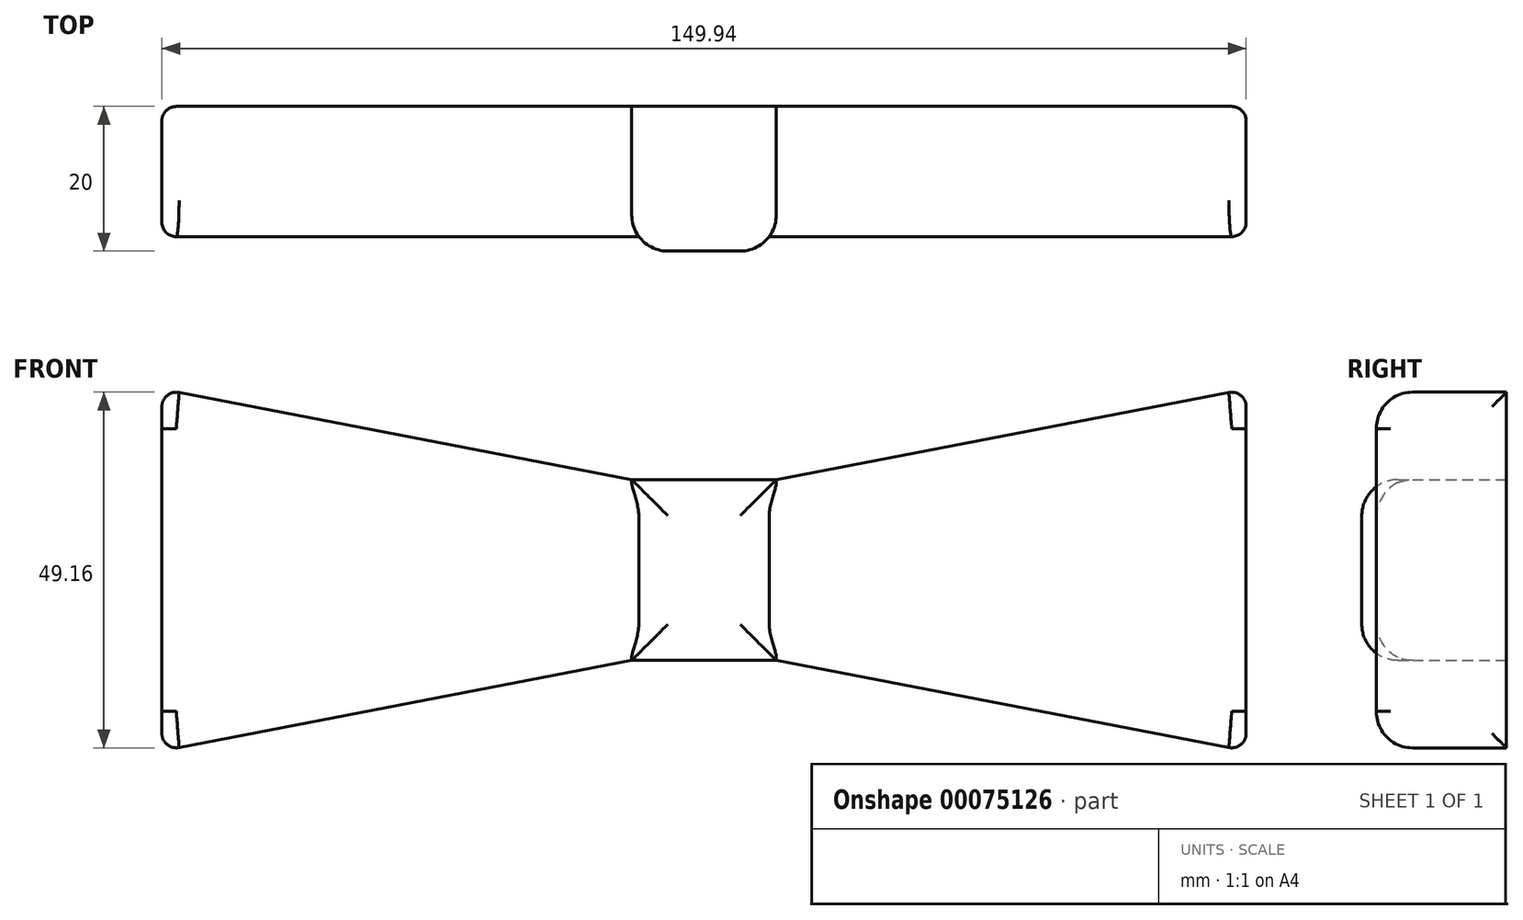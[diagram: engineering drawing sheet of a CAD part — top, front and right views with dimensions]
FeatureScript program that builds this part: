
annotation { "Feature Type Name" : "Feature", "Feature Type Description" : "" }
export const myFeature = defineFeature(function(context is Context, id is Id, definition is map)
    precondition{}
    {
        {
            var Q0;
            Q0=qCreatedBy(makeId("Front.planeOp"),FACE);
            var sketch = newSketch(context, id + "F0", { "sketchPlane" : qUnion([Q0])});
            skLineSegment(sketch, "E0.rect.bottom", {"start": v(10, -12.5) * mm, "end": v(-10, -12.5) * mm});
            skLineSegment(sketch, "E0.rect.top", {"start": v(10, 12.5) * mm, "end": v(-10, 12.5) * mm});
            skLineSegment(sketch, "E0.rect.left", {"start": v(10, -12.5) * mm, "end": v(10, 12.5) * mm});
            skLineSegment(sketch, "E0.rect.right", {"start": v(-10, -12.5) * mm, "end": v(-10, 12.5) * mm});
            skPoint(sketch, "E0.rect.middle", {"position": v(0, 0) * mm});
            skLineSegment(sketch, "E1", {"start": v(-10, 12.5) * mm, "end": v(-74.97, 25) * mm});
            skLineSegment(sketch, "E2", {"start": v(-74.97, 25) * mm, "end": v(-74.97, -25) * mm});
            skLineSegment(sketch, "E3", {"start": v(-74.97, -25) * mm, "end": v(-10, -12.5) * mm});
            skLineSegment(sketch, "E4.MirrorCS", {"start": v(10, 12.5) * mm, "end": v(74.97, 25) * mm});
            skLineSegment(sketch, "E5.MirrorCS", {"start": v(74.97, 25) * mm, "end": v(74.97, -25) * mm});
            skLineSegment(sketch, "E6.MirrorCS", {"start": v(74.97, -25) * mm, "end": v(10, -12.5) * mm});
            skSolve(sketch);
        }
        {
            var Q0;
            Q0=makeQuery(id+"F0.imprint","IMPRINT",FACE,{"disambiguationData":[TD([[makeQuery(id+"F0.imprint","IMPRINT",EDGE,{"derivedFrom":sQuery(id+"F0.wireOp",EDGE,"E0.rect.bottom")}),-1.0]])]});
            extrude(context, id + "F1", {"entities" : qUnion([Q0]), "depth" : 20 * mm});
        }
        {
            var Q0;
            Q0=makeQuery(id+"F0.imprint","IMPRINT",FACE,{"disambiguationData":[TD([[makeQuery(id+"F0.imprint","IMPRINT",EDGE,{"derivedFrom":sQuery(id+"F0.wireOp",EDGE,"E0.rect.left")}),-1.0]])]});
            var Q1;
            Q1=makeQuery(id+"F0.imprint","IMPRINT",FACE,{"disambiguationData":[TD([[makeQuery(id+"F0.imprint","IMPRINT",EDGE,{"derivedFrom":sQuery(id+"F0.wireOp",EDGE,"E0.rect.right")}),1.0]])]});
            extrude(context, id + "F2", {"entities" : qUnion([Q0, Q1]), "operationType" : NewBodyOperationType.ADD, "depth" : 18 * mm});
        }
        {
            var Q0;
            Q0=makeQuery(id+"F2.opExtrude","CAP_EDGE",EDGE,{"disambiguationData":[OSD([sQuery(id+"F0.wireOp",EDGE,"E1")])],"isStart":false});
            var Q1;
            Q1=makeQuery(id+"F2.opExtrude","CAP_EDGE",EDGE,{"disambiguationData":[OSD([sQuery(id+"F0.wireOp",EDGE,"E4.MirrorCS")])],"isStart":false});
            var Q2;
            Q2=makeQuery(id+"F2.opExtrude","CAP_EDGE",EDGE,{"disambiguationData":[OSD([sQuery(id+"F0.wireOp",EDGE,"E6.MirrorCS")])],"isStart":false});
            var Q3;
            Q3=makeQuery(id+"F2.opExtrude","CAP_EDGE",EDGE,{"disambiguationData":[OSD([sQuery(id+"F0.wireOp",EDGE,"E3")])],"isStart":false});
            fillet(context, id + "F3", {"entities" : qUnion([Q0, Q1, Q2, Q3]), "radius" : 5 * mm, "tangentPropagation" : true, "allowEdgeOverflow" : false});
        }
        {
            var Q0;
            Q0=makeQuery(id+"F1.opExtrude","CAP_EDGE",EDGE,{"disambiguationData":[OSD([sQuery(id+"F0.wireOp",EDGE,"E0.rect.top")])],"isStart":false});
            var Q1;
            Q1=makeQuery(id+"F1.opExtrude","CAP_EDGE",EDGE,{"disambiguationData":[OSD([sQuery(id+"F0.wireOp",EDGE,"E0.rect.bottom")])],"isStart":false});
            var Q2;
            Q2=makeQuery(id+"F1.opExtrude","CAP_EDGE",EDGE,{"disambiguationData":[OSD([sQuery(id+"F0.wireOp",EDGE,"E0.rect.left")])],"isStart":false});
            var Q3;
            Q3=makeQuery(id+"F1.opExtrude","CAP_EDGE",EDGE,{"disambiguationData":[OSD([sQuery(id+"F0.wireOp",EDGE,"E0.rect.right")])],"isStart":false});
            fillet(context, id + "F4", {"entities" : qUnion([Q0, Q1, Q2, Q3]), "radius" : 5 * mm, "tangentPropagation" : true, "allowEdgeOverflow" : false});
        }
        {
            var Q0;
            Q0=makeQuery(id+"F2.opExtrude","SWEPT_FACE",FACE,{"disambiguationData":[OSD([sQuery(id+"F0.wireOp",EDGE,"E5.MirrorCS")])]});
            var Q1;
            Q1=makeQuery(id+"F2.opExtrude","SWEPT_FACE",FACE,{"disambiguationData":[OSD([sQuery(id+"F0.wireOp",EDGE,"E2")])]});
            fillet(context, id + "F5", {"entities" : qUnion([Q0, Q1]), "radius" : 2 * mm, "tangentPropagation" : true, "allowEdgeOverflow" : false});
        }
    });
